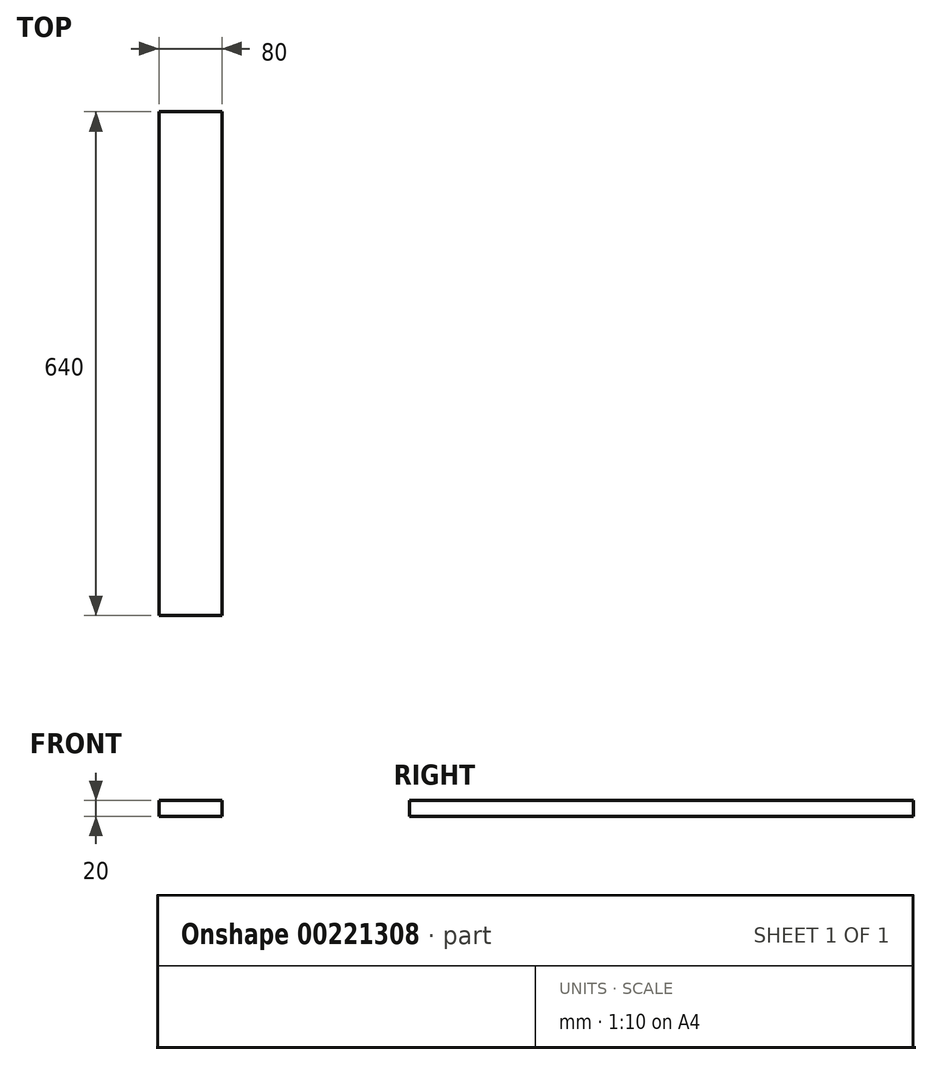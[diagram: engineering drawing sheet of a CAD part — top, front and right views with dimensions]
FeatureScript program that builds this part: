
annotation { "Feature Type Name" : "Feature", "Feature Type Description" : "" }
export const myFeature = defineFeature(function(context is Context, id is Id, definition is map)
    precondition{}
    {
        {
            var Q0;
            Q0=qCreatedBy(makeId("Front.planeOp"),FACE);
            var sketch = newSketch(context, id + "F0", { "sketchPlane" : qUnion([Q0])});
            skLineSegment(sketch, "E0.bottom", {"start": v(-35, 9.84) * mm, "end": v(45, 9.84) * mm});
            skLineSegment(sketch, "E0.top", {"start": v(-35, -10.16) * mm, "end": v(45, -10.16) * mm});
            skLineSegment(sketch, "E0.left", {"start": v(-35, 9.84) * mm, "end": v(-35, -10.16) * mm});
            skLineSegment(sketch, "E0.right", {"start": v(45, 9.84) * mm, "end": v(45, -10.16) * mm});
            skSolve(sketch);
        }
        {
            var Q0;
            Q0=makeQuery(id+"F0.imprint","IMPRINT",FACE,{"disambiguationData":[TD([[makeQuery(id+"F0.imprint","IMPRINT",EDGE,{"derivedFrom":sQuery(id+"F0.wireOp",EDGE,"E0.bottom")}),-1.0]])]});
            extrude(context, id + "F1", {"entities" : qUnion([Q0]), "oppositeDirection" : true, "depth" : 640 * mm});
        }
    });
